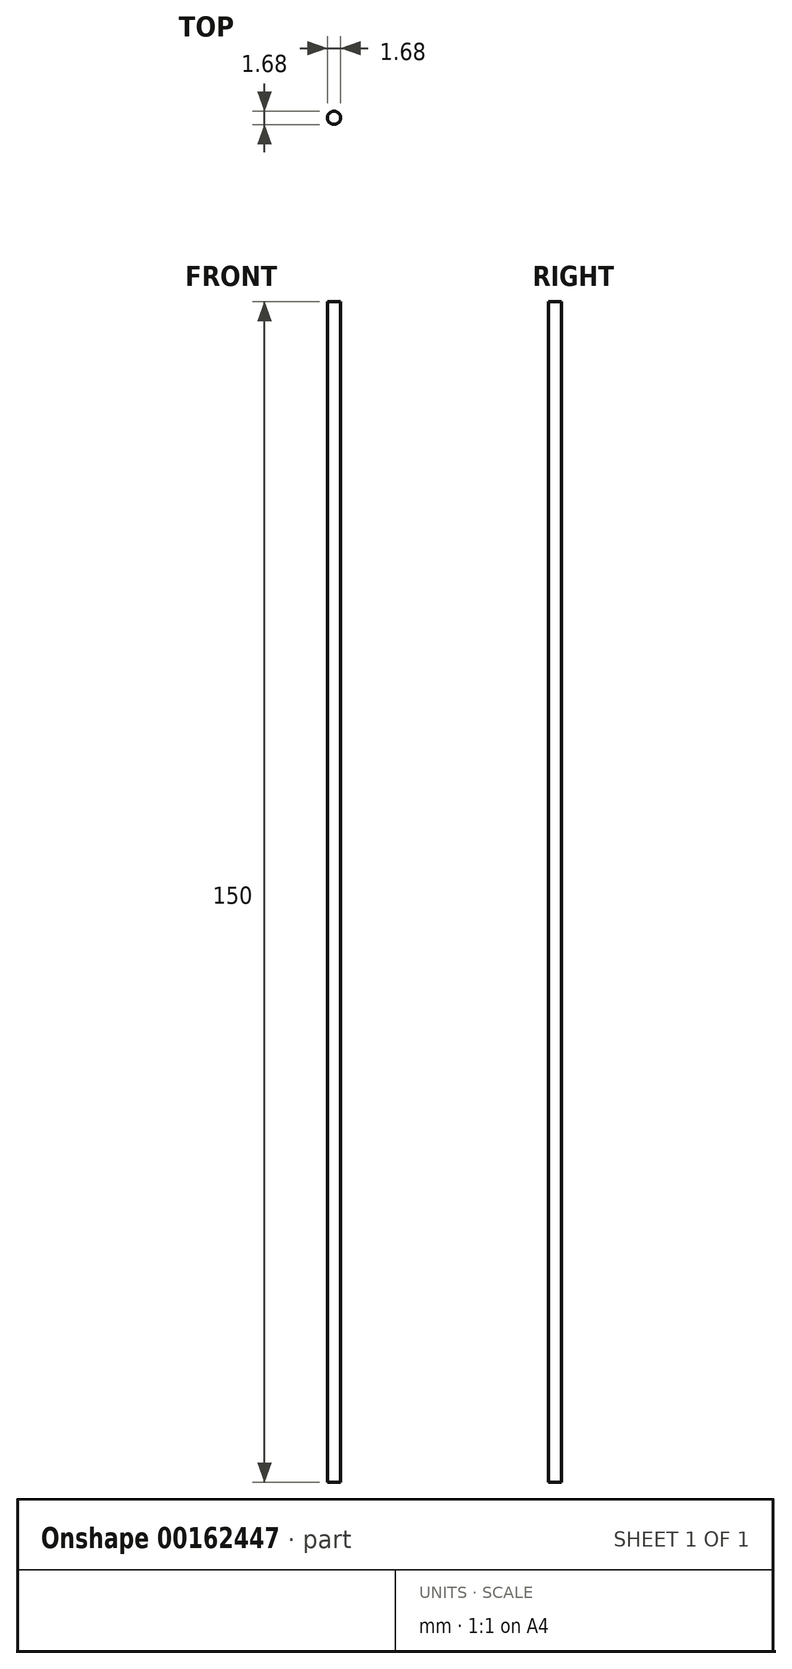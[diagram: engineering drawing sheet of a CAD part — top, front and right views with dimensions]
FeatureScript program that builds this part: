
annotation { "Feature Type Name" : "Feature", "Feature Type Description" : "" }
export const myFeature = defineFeature(function(context is Context, id is Id, definition is map)
    precondition{}
    {
        {
            var Q0;
            Q0=qCreatedBy(makeId("Top.planeOp"),FACE);
            var sketch = newSketch(context, id + "F0", { "sketchPlane" : qUnion([Q0])});
            skCircle(sketch, "E0", {"center": v(0, 0) * mm, "radius": 0.84 * mm});
            skSolve(sketch);
        }
        {
            var Q0;
            Q0 = qSketchRegion(id + "F0", true);
            extrude(context, id + "F1", {"entities" : qUnion([Q0]), "depth" : 150 * mm});
        }
    });
